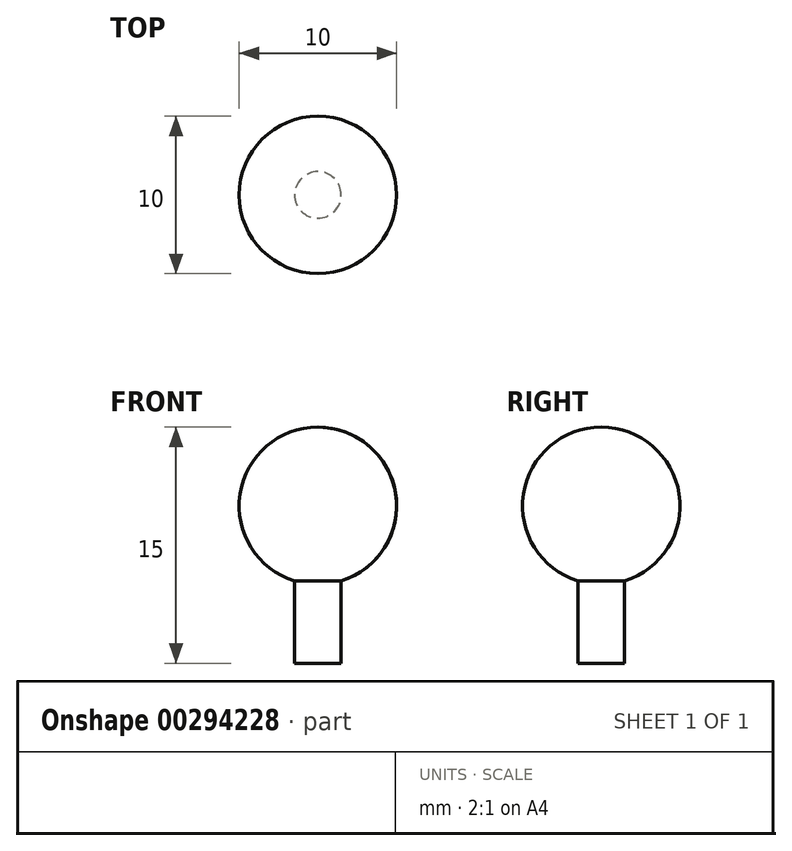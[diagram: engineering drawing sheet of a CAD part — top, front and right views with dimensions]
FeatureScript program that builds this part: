
annotation { "Feature Type Name" : "Feature", "Feature Type Description" : "" }
export const myFeature = defineFeature(function(context is Context, id is Id, definition is map)
    precondition{}
    {
        {
            var Q0;
            Q0=qCreatedBy(makeId("Front.planeOp"),FACE);
            var sketch = newSketch(context, id + "F0", { "sketchPlane" : qUnion([Q0])});
            skArc(sketch, "E0", {"start": v(1.48, -4.78) * mm, "mid": v(4.94, 0.75) * mm, "end": v(0, 5) * mm});
            skLineSegment(sketch, "E1.top", {"start": v(0, -10) * mm, "end": v(1.48, -10) * mm});
            skLineSegment(sketch, "E1.right", {"start": v(1.48, -4.78) * mm, "end": v(1.48, -10) * mm});
            skPoint(sketch, "E2.orphan", {"position": v(-1.48, 10) * mm});
            skPoint(sketch, "E3.orphan", {"position": v(1.48, 10) * mm});
            skLineSegment(sketch, "E4", {"start": v(0, 5) * mm, "end": v(0, -10) * mm});
            skPoint(sketch, "E5.orphan", {"position": v(-1.48, -10) * mm});
            skLineSegment(sketch, "E6", {"start": v(0, 6.34) * mm, "end": v(0, -11.2) * mm});
            skSolve(sketch);
        }
        {
            var Q0;
            Q0 = qSketchRegion(id + "F0", true);
            var Q1;
            Q1=sQuery(id+"F0.wireOp",EDGE,"E6");
            revolve(context, id + "F1", {"entities" : qUnion([Q0]), "axis" : qUnion([Q1]), "revolveType" : RevolveType.FULL});
        }
    });
